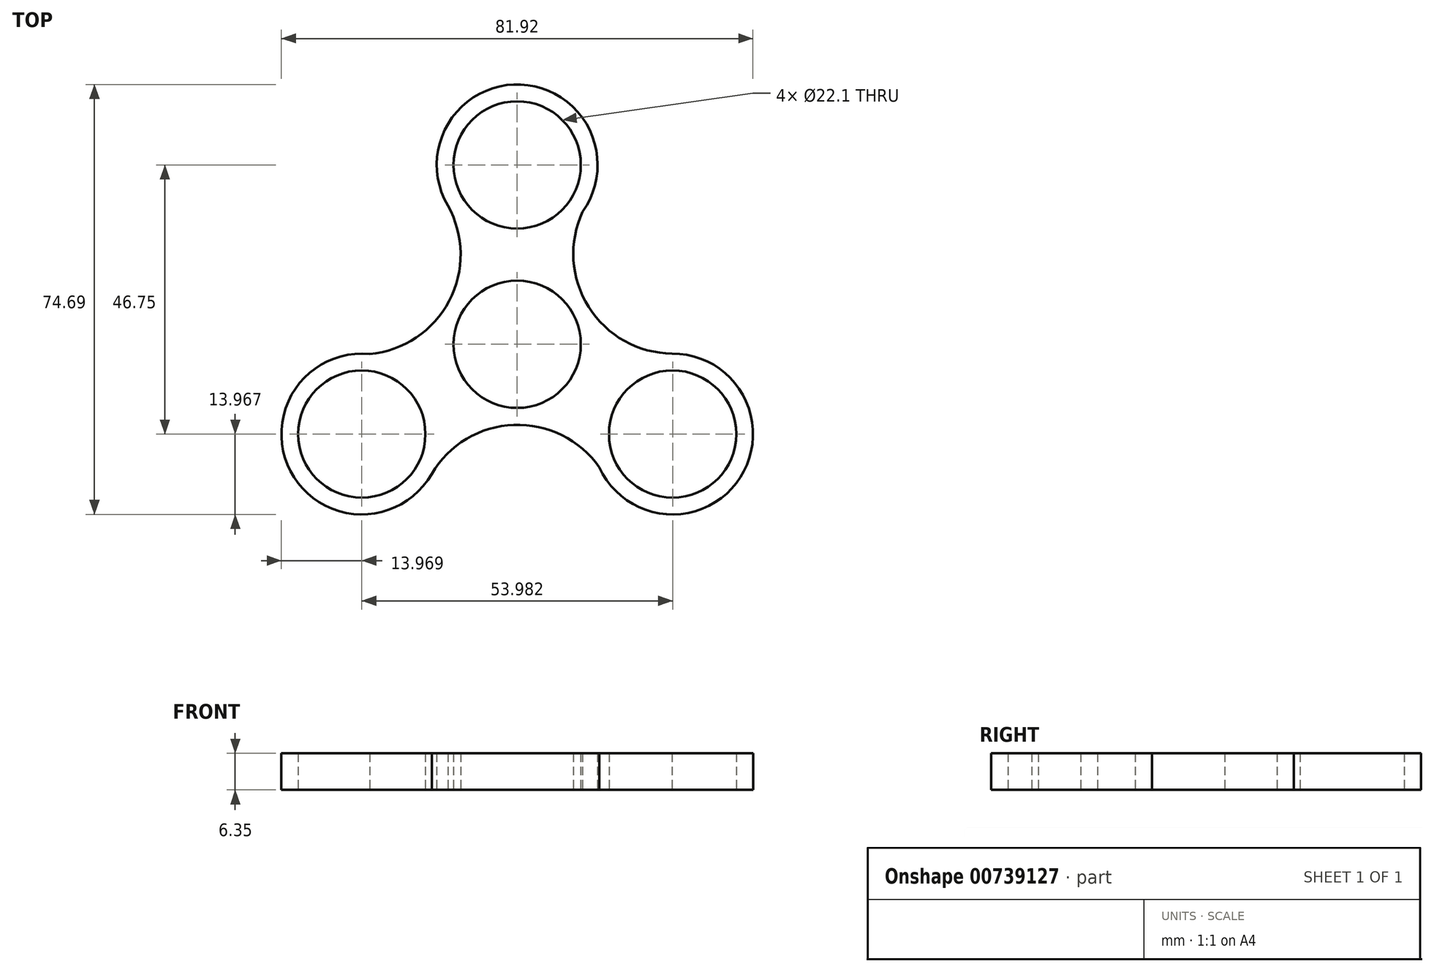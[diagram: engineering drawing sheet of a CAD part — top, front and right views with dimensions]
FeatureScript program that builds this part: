
annotation { "Feature Type Name" : "Feature", "Feature Type Description" : "" }
export const myFeature = defineFeature(function(context is Context, id is Id, definition is map)
    precondition{}
    {
        {
            var Q0;
            Q0=qCreatedBy(makeId("Top.planeOp"),FACE);
            var sketch = newSketch(context, id + "F0", { "sketchPlane" : qUnion([Q0])});
            skCircle(sketch, "E0", {"center": v(0, 0) * mm, "radius": 11.05 * mm});
            skCircle(sketch, "E1", {"center": v(0, 31.17) * mm, "radius": 11.05 * mm});
            skCircle(sketch, "E2", {"center": v(0, 31.17) * mm, "radius": 13.97 * mm});
            skCircle(sketch, "E3.1.0", {"center": v(-27, -15.58) * mm, "radius": 11.05 * mm});
            skCircle(sketch, "E3.1.1", {"center": v(-27, -15.58) * mm, "radius": 13.97 * mm});
            skCircle(sketch, "E3.2.0", {"center": v(27, -15.58) * mm, "radius": 11.05 * mm});
            skCircle(sketch, "E3.2.1", {"center": v(27, -15.58) * mm, "radius": 13.97 * mm});
            skArc(sketch, "E4", {"start": v(11.37, 23.05) * mm, "mid": v(12.49, 6.38) * mm, "end": v(27.16, -1.61) * mm});
            skArc(sketch, "E5.1.0", {"start": v(-25.64, -1.68) * mm, "mid": v(-11.77, 7.62) * mm, "end": v(-12.18, 24.33) * mm});
            skArc(sketch, "E5.2.0", {"start": v(14.27, -21.37) * mm, "mid": v(-0.72, -14) * mm, "end": v(-14.98, -22.71) * mm});
            skSolve(sketch);
        }
        {
            var Q0;
            Q0 = qSketchRegion(id + "F0", true);
            extrude(context, id + "F1", {"entities" : qUnion([Q0]), "depth" : 6.35 * mm, "offsetDistance" : 25.4 * mm});
        }
        {
            var Q0;
            Q0 = qSketchRegion(id + "F0", true);
            extrude(context, id + "F2", {"entities" : qUnion([Q0]), "operationType" : NewBodyOperationType.ADD, "depth" : 6.35 * mm, "offsetDistance" : 25.4 * mm});
        }
    });
